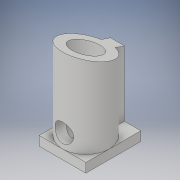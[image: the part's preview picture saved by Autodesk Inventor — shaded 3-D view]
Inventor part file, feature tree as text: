
AUTODESK INVENTOR PART (.ipt)
format: ipt  version: 2019 (Build 230136000, 136)  size: 147,968 bytes
history: native  units: mm
features: extrude x4, sketch x4, projected_geometry x1
ambient origin geometry x8: Origin, YZ Plane, XZ Plane, XY Plane, X Axis, Y Axis, Z Axis, Center Point
bodies: Solide1 (feature_tree)
feature tree (9):
  extrude  "Extrusion1"  Depth=5.0mm
  extrude  "Extrusion2"  Depth=1.5mm
  extrude  "Extrusion3"  Depth=1.0mm
  extrude  "Extrusion4"  Depth=3.0mm
  sketch  "Esquisse1"
  sketch  "Esquisse2"
  projected_geometry  "Boucle projetée1"
  sketch  "Esquisse3"
  sketch  "Esquisse4"
